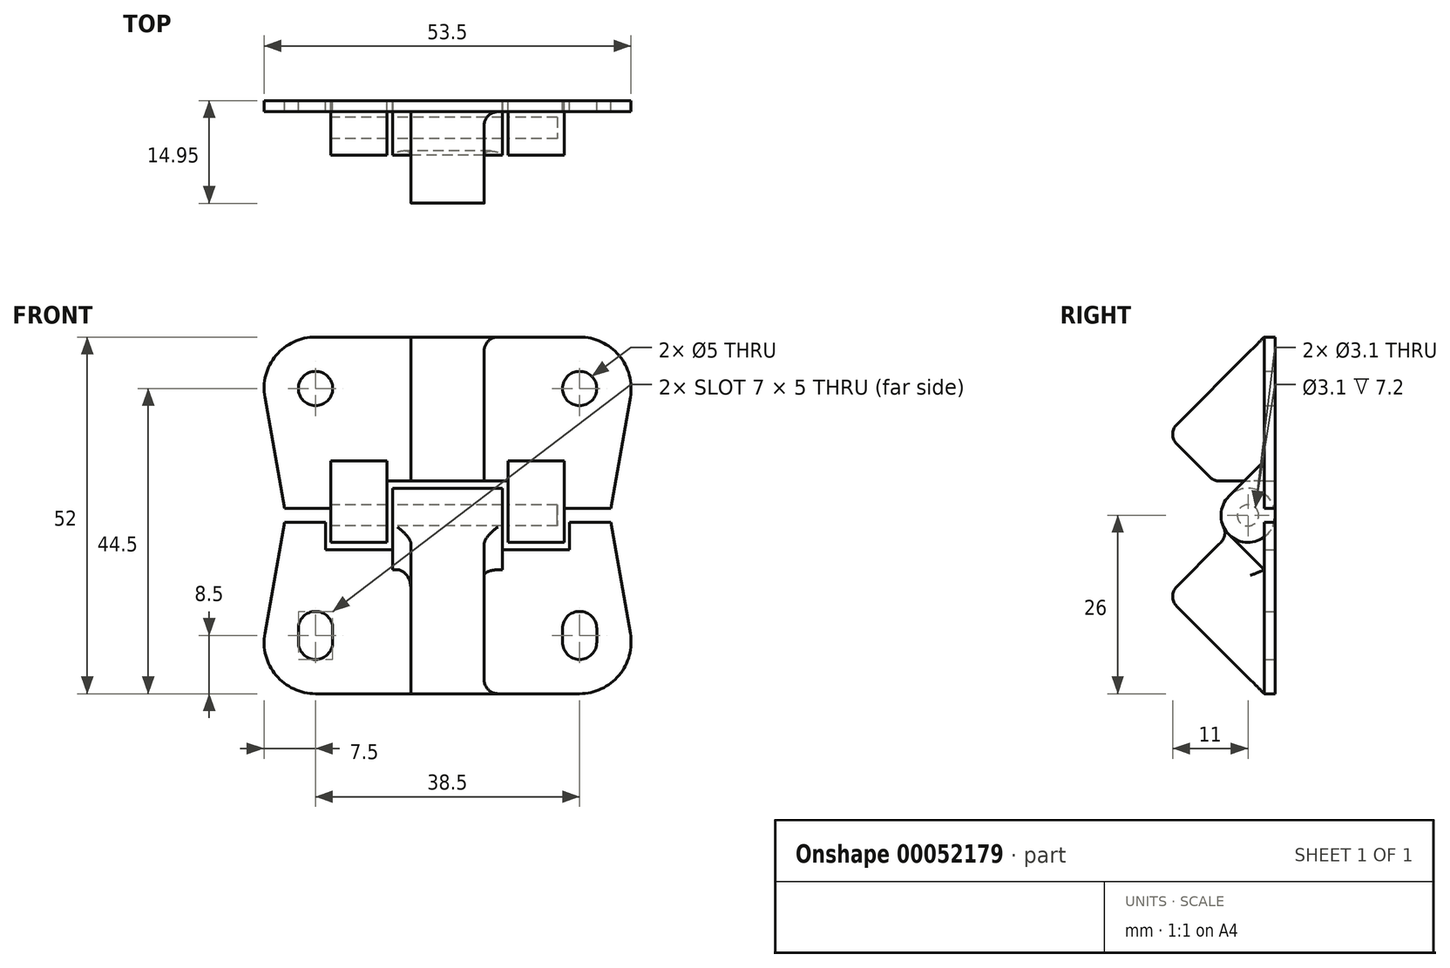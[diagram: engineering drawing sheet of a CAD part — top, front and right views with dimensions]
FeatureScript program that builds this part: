
annotation { "Feature Type Name" : "Feature", "Feature Type Description" : "" }
export const myFeature = defineFeature(function(context is Context, id is Id, definition is map)
    precondition{}
    {
        {
            assignVariable(context, id + "F0", {"name" : "pin_length", "anyValue" : 32});
        }
        {
            var Q0;
            Q0=qCreatedBy(makeId("Front.planeOp"),FACE);
            var sketch = newSketch(context, id + "F1", { "sketchPlane" : qUnion([Q0])});
            skCircle(sketch, "E0", {"center": v(0, 0) * mm, "radius": 2.5 * mm});
            skCircle(sketch, "E1", {"center": v(-38.5, 0) * mm, "radius": 2.5 * mm});
            skArc(sketch, "E2", {"start": v(2.5, -35) * mm, "mid": v(0, -32.5) * mm, "end": v(-2.5, -35) * mm});
            skArc(sketch, "E3", {"start": v(-36, -35) * mm, "mid": v(-38.5, -32.5) * mm, "end": v(-41, -35) * mm});
            skArc(sketch, "E4", {"start": v(-41, -37) * mm, "mid": v(-38.5, -39.5) * mm, "end": v(-36, -37) * mm});
            skArc(sketch, "E5", {"start": v(-2.5, -37) * mm, "mid": v(0, -39.5) * mm, "end": v(2.5, -37) * mm});
            skLineSegment(sketch, "E6", {"start": v(-41, -35) * mm, "end": v(-41, -37) * mm});
            skLineSegment(sketch, "E7", {"start": v(-36, -35) * mm, "end": v(-36, -37) * mm});
            skLineSegment(sketch, "E8", {"start": v(-2.5, -35) * mm, "end": v(-2.5, -37) * mm});
            skLineSegment(sketch, "E9", {"start": v(2.5, -35) * mm, "end": v(2.5, -37) * mm});
            skLineSegment(sketch, "E10", {"start": v(-38.5, 7.5) * mm, "end": v(0, 7.5) * mm});
            skLineSegment(sketch, "E11", {"start": v(0, -44.5) * mm, "end": v(-38.5, -44.5) * mm});
            skLineSegment(sketch, "E12", {"start": v(-45.89, -1.3) * mm, "end": v(-43.03, -17.5) * mm});
            skLineSegment(sketch, "E13", {"start": v(-42.85, -18.5) * mm, "end": v(-43.03, -19.5) * mm});
            skLineSegment(sketch, "E14", {"start": v(7.39, -1.3) * mm, "end": v(4.35, -18.5) * mm});
            skLineSegment(sketch, "E15", {"start": v(4.35, -18.5) * mm, "end": v(7.39, -35.7) * mm});
            skPoint(sketch, "E16.visualSharp", {"position": v(-47.44, 7.5) * mm});
            skArc(sketch, "E16.filletArc", {"start": v(-38.5, 7.5) * mm, "mid": v(-44.25, 4.82) * mm, "end": v(-45.89, -1.3) * mm});
            skPoint(sketch, "E17.visualSharp", {"position": v(-47.44, -44.5) * mm});
            skArc(sketch, "E17.filletArc", {"start": v(-45.89, -35.7) * mm, "mid": v(-44.25, -41.82) * mm, "end": v(-38.5, -44.5) * mm});
            skPoint(sketch, "E18.visualSharp", {"position": v(8.94, -44.5) * mm});
            skArc(sketch, "E18.filletArc", {"start": v(0, -44.5) * mm, "mid": v(5.75, -41.82) * mm, "end": v(7.39, -35.7) * mm});
            skPoint(sketch, "E19.visualSharp", {"position": v(8.94, 7.5) * mm});
            skArc(sketch, "E19.filletArc", {"start": v(7.39, -1.3) * mm, "mid": v(5.75, 4.82) * mm, "end": v(0, 7.5) * mm});
            skLineSegment(sketch, "E20", {"start": v(-42.85, -18.5) * mm, "end": v(4.35, -18.5) * mm, "construction": true});
            skLineSegment(sketch, "E21", {"start": v(-43.03, -17.5) * mm, "end": v(4.53, -17.5) * mm});
            skLineSegment(sketch, "E22", {"start": v(4.53, -19.5) * mm, "end": v(-43.03, -19.5) * mm});
            skLineSegment(sketch, "E23", {"start": v(-43.03, -17.5) * mm, "end": v(-42.85, -18.5) * mm});
            skLineSegment(sketch, "E24", {"start": v(-43.03, -19.5) * mm, "end": v(-45.89, -35.7) * mm});
            skLineSegment(sketch, "E25", {"start": v(-19.25, 7.5) * mm, "end": v(-19.25, -44.5) * mm, "construction": true});
            skLineSegment(sketch, "E26.bottom", {"start": v(-28.05, -17.5) * mm, "end": v(-10.45, -17.5) * mm});
            skLineSegment(sketch, "E26.top", {"start": v(-28.05, -13.5) * mm, "end": v(-19.25, -13.5) * mm});
            skLineSegment(sketch, "E26.left", {"start": v(-28.05, -17.5) * mm, "end": v(-28.05, -13.5) * mm});
            skLineSegment(sketch, "E26.right", {"start": v(-10.45, -17.5) * mm, "end": v(-10.45, -13.5) * mm});
            skLineSegment(sketch, "E27", {"start": v(-19.25, -13.5) * mm, "end": v(-10.45, -13.5) * mm});
            skLineSegment(sketch, "E28.bottom", {"start": v(-37.05, -19.5) * mm, "end": v(-1.45, -19.5) * mm});
            skLineSegment(sketch, "E28.top", {"start": v(-37.05, -23.5) * mm, "end": v(-19.25, -23.5) * mm});
            skLineSegment(sketch, "E28.left", {"start": v(-37.05, -19.5) * mm, "end": v(-37.05, -23.5) * mm});
            skLineSegment(sketch, "E28.right", {"start": v(-1.45, -19.5) * mm, "end": v(-1.45, -23.5) * mm});
            skLineSegment(sketch, "E29", {"start": v(-19.25, -23.5) * mm, "end": v(-1.45, -23.5) * mm});
            skSolve(sketch);
        }
        {
            var Q0;
            Q0=makeQuery(id+"F1.imprint","IMPRINT",FACE,{"disambiguationData":[TD([[makeQuery(id+"F1.imprint","IMPRINT",EDGE,{"derivedFrom":sQuery(id+"F1.wireOp",EDGE,"E0")}),-1.0]])]});
            var Q1;
            Q1=makeQuery(id+"F1.imprint","IMPRINT",FACE,{"disambiguationData":[TD([[makeQuery(id+"F1.imprint","IMPRINT",EDGE,{"derivedFrom":sQuery(id+"F1.wireOp",EDGE,"E2")}),-1.0]])]});
            extrude(context, id + "F2", {"entities" : qUnion([Q0, Q1]), "depth" : (0.4 * 4) * mm});
        }
        {
            var Q0;
            Q0=sQuery(id+"F1.wireOp",EDGE,"E25");
            var Q1;
            Q1=qCreatedBy(makeId("Right.planeOp"),FACE);
            cPlane(context, id + "F3", {"entities" : qUnion([Q0, Q1]), "cplaneType" : CPlaneType.LINE_ANGLE, "offset" : 150 * mm, "angle" : 180 * degree, "width" : 150 * mm, "height" : 150 * mm});
        }
        {
            var Q0;
            Q0=qCreatedBy(id+"F3.planeOp",FACE);
            var sketch = newSketch(context, id + "F4", { "sketchPlane" : qUnion([Q0])});
            skCircle(sketch, "E30", {"center": v(-3.95, -18.5) * mm, "radius": 3.95 * mm});
            skCircle(sketch, "E31", {"center": v(-3.95, -18.5) * mm, "radius": 1.55 * mm});
            skSolve(sketch);
        }
        {
            var Q0;
            Q0=makeQuery(id+"F4.imprint","IMPRINT",FACE,{"disambiguationData":[TD([[makeQuery(id+"F4.imprint","IMPRINT",EDGE,{"derivedFrom":sQuery(id+"F4.wireOp",EDGE,"E30")}),1.0]])]});
            extrude(context, id + "F5", {"entities" : qUnion([Q0]), "endBound" : BoundingType.SYMMETRIC, "depth" : (getVariable(context, 'pin_length') + 2) * mm});
        }
        {
            var Q0;
            Q0=makeQuery(id+"F4.imprint","IMPRINT",FACE,{"disambiguationData":[TD([[makeQuery(id+"F4.imprint","IMPRINT",EDGE,{"derivedFrom":sQuery(id+"F4.wireOp",EDGE,"E30")}),1.0]])]});
            extrude(context, id + "F6", {"entities" : qUnion([Q0]), "endBound" : BoundingType.SYMMETRIC, "depth" : (getVariable(context, 'pin_length') / 2) * mm});
        }
        {
            var Q0;
            Q0=makeQuery(id+"F6.opExtrude","SWEPT_BODY",BODY,{"disambiguationData":[OSD([sQuery(id+"F4.wireOp",EDGE,"E30"),sQuery(id+"F4.wireOp",EDGE,"E31")])]});
            var Q1;
            Q1=makeQuery(id+"F5.opExtrude","SWEPT_BODY",BODY,{"disambiguationData":[OSD([sQuery(id+"F4.wireOp",EDGE,"E30"),sQuery(id+"F4.wireOp",EDGE,"E31")])]});
            booleanBodies(context, id + "F7", {"operationType" : BooleanOperationType.SUBTRACTION, "tools" : qUnion([Q0]), "targets" : qUnion([Q1]), "offset" : true, "offsetAll" : true, "offsetDistance" : .8 * mm, "keepTools" : true});
        }
        {
            var Q0;
            Q0=makeQuery(id+"F5.opExtrude","CAP_FACE",FACE,{"disambiguationData":[OSD([sQuery(id+"F4.wireOp",EDGE,"E30"),sQuery(id+"F4.wireOp",EDGE,"E31")])],"isStart":false});
            var sketch = newSketch(context, id + "F8", { "sketchPlane" : qUnion([Q0])});
            skLineSegment(sketch, "E32", {"start": v(0, -18.5) * mm, "end": v(0, -8.96) * mm});
            skLineSegment(sketch, "E33", {"start": v(0, -8.96) * mm, "end": v(-6.74, -15.7) * mm});
            skLineSegment(sketch, "E34", {"start": v(-3.95, -18.5) * mm, "end": v(4.49, -18.5) * mm, "construction": true});
            skLineSegment(sketch, "E35", {"start": v(-6.74, -21.3) * mm, "end": v(0, -28.04) * mm});
            skLineSegment(sketch, "E36", {"start": v(0, -28.04) * mm, "end": v(0, -18.5) * mm});
            skCircle(sketch, "E37", {"center": v(-3.95, -18.5) * mm, "radius": 1.55 * mm});
            skSolve(sketch);
        }
        {
            var Q0;
            {var subQ6=sQuery(id+"F8.wireOp",EDGE,"E32");Q0=makeQuery(id+"F8.imprint","IMPRINT",FACE,{"disambiguationData":[TD([[makeQuery(id+"F8.imprint","IMPRINT",EDGE,{"derivedFrom":subQ6}),1.0]])]});}
            var Q1;
            Q1=makeQuery(id+"F7.tempBoolean.opBoolean","COPY",FACE,{"derivedFrom":makeQuery(id+"F7.offsetTempBody.opPattern","COPY",FACE,{"derivedFrom":makeQuery(id+"F6.opExtrude","CAP_FACE",FACE,{"disambiguationData":[OSD([sQuery(id+"F4.wireOp",EDGE,"E30"),sQuery(id+"F4.wireOp",EDGE,"E31")])],"isStart":false}),"instanceName":"1"})});
            var Q2;
            Q2=makeQuery(id+"F2.opExtrude","SWEPT_BODY",BODY,{"disambiguationData":[OSD([sQuery(id+"F1.wireOp",EDGE,"E0"),sQuery(id+"F1.wireOp",EDGE,"E1"),sQuery(id+"F1.wireOp",EDGE,"E10"),sQuery(id+"F1.wireOp",EDGE,"E12"),sQuery(id+"F1.wireOp",EDGE,"E14"),sQuery(id+"F1.wireOp",EDGE,"E16.filletArc"),sQuery(id+"F1.wireOp",EDGE,"E19.filletArc"),sQuery(id+"F1.wireOp",EDGE,"E21")])]});
            var Q3;
            Q3=makeQuery(id+"F5.opExtrude","CAP_FACE",FACE,{"disambiguationData":[OSD([sQuery(id+"F4.wireOp",EDGE,"E30"),sQuery(id+"F4.wireOp",EDGE,"E31")])],"isStart":true});
            extrude(context, id + "F9", {"entities" : qUnion([Q0]), "operationType" : NewBodyOperationType.ADD, "endBound" : BoundingType.UP_TO_SURFACE, "oppositeDirection" : true, "endBoundEntityFace" : qUnion([Q1]), "endBoundEntityBody" : qUnion([Q2]), "depth" : 25 * mm});
        }
        {
            var Q0;
            {var subQ6=sQuery(id+"F8.wireOp",EDGE,"E32");Q0=makeQuery(id+"F8.imprint","IMPRINT",FACE,{"disambiguationData":[TD([[makeQuery(id+"F8.imprint","IMPRINT",EDGE,{"derivedFrom":subQ6}),1.0]])]});}
            var Q1;
            Q1=makeQuery(id+"F5.opExtrude","CAP_FACE",FACE,{"disambiguationData":[OSD([sQuery(id+"F4.wireOp",EDGE,"E30"),sQuery(id+"F4.wireOp",EDGE,"E31")])],"isStart":true});
            var Q2;
            Q2=makeQuery(id+"F7.tempBoolean.opBoolean","COPY",FACE,{"derivedFrom":makeQuery(id+"F7.offsetTempBody.opPattern","COPY",FACE,{"derivedFrom":makeQuery(id+"F6.opExtrude","CAP_FACE",FACE,{"disambiguationData":[OSD([sQuery(id+"F4.wireOp",EDGE,"E30"),sQuery(id+"F4.wireOp",EDGE,"E31")])],"isStart":true}),"instanceName":"1"})});
            extrude(context, id + "F10", {"entities" : qUnion([Q0]), "operationType" : NewBodyOperationType.ADD, "endBound" : BoundingType.UP_TO_SURFACE, "oppositeDirection" : true, "endBoundEntityFace" : qUnion([Q1]), "depth" : 25 * mm, "hasSecondDirection" : true, "secondDirectionBound" : SecondDirectionBoundingType.UP_TO_SURFACE, "secondDirectionOppositeDirection" : true, "secondDirectionBoundEntityFace" : qUnion([Q2]), "secondDirectionDepth" : 45.6 * mm});
        }
        {
            var Q0;
            {var subQ0=sQuery(id+"F8.wireOp",EDGE,"E35");Q0=makeQuery(id+"F8.imprint","IMPRINT",FACE,{"disambiguationData":[TD([[makeQuery(id+"F8.imprint","IMPRINT",EDGE,{"derivedFrom":subQ0}),1.0]])]});}
            var Q1;
            Q1=makeQuery(id+"F6.opExtrude","CAP_FACE",FACE,{"disambiguationData":[OSD([sQuery(id+"F4.wireOp",EDGE,"E30"),sQuery(id+"F4.wireOp",EDGE,"E31")])],"isStart":true});
            var Q2;
            Q2=makeQuery(id+"F6.opExtrude","CAP_FACE",FACE,{"disambiguationData":[OSD([sQuery(id+"F4.wireOp",EDGE,"E30"),sQuery(id+"F4.wireOp",EDGE,"E31")])],"isStart":false});
            extrude(context, id + "F11", {"entities" : qUnion([Q0]), "operationType" : NewBodyOperationType.ADD, "endBound" : BoundingType.UP_TO_SURFACE, "oppositeDirection" : true, "endBoundEntityFace" : qUnion([Q1]), "depth" : 25 * mm, "hasSecondDirection" : true, "secondDirectionBound" : SecondDirectionBoundingType.UP_TO_SURFACE, "secondDirectionOppositeDirection" : true, "secondDirectionBoundEntityFace" : qUnion([Q2]), "secondDirectionDepth" : 25 * mm});
        }
        {
            var Q0;
            Q0=makeQuery(id+"F8.imprint","IMPRINT",FACE,{"disambiguationData":[TD([[makeQuery(id+"F8.imprint","IMPRINT",EDGE,{"derivedFrom":sQuery(id+"F8.wireOp",EDGE,"E37")}),1.0]])]});
            extrude(context, id + "F12", {"entities" : qUnion([Q0]), "operationType" : NewBodyOperationType.ADD, "oppositeDirection" : true, "depth" : 1 * mm});
        }
        {
            var Q0;
            Q0=qCreatedBy(id+"F3.planeOp",FACE);
            var sketch = newSketch(context, id + "F13", { "sketchPlane" : qUnion([Q0])});
            skLineSegment(sketch, "E38", {"start": v(-3.95, -18.5) * mm, "end": v(-15.78, -6.68) * mm});
            skLineSegment(sketch, "E39", {"start": v(-15.77, -30.33) * mm, "end": v(-3.95, -18.5) * mm});
            skLineSegment(sketch, "E40", {"start": v(-1.6, 7.5) * mm, "end": v(-15.78, -6.68) * mm});
            skLineSegment(sketch, "E41", {"start": v(-1.6, -44.5) * mm, "end": v(-15.77, -30.33) * mm});
            skLineSegment(sketch, "E42", {"start": v(-8.95, -13.5) * mm, "end": v(-1.6, -13.5) * mm});
            skLineSegment(sketch, "E43", {"start": v(-1.6, 7.5) * mm, "end": v(-1.6, -13.5) * mm});
            skLineSegment(sketch, "E44", {"start": v(-6.74, -21.3) * mm, "end": v(-1.6, -21.3) * mm});
            skLineSegment(sketch, "E45", {"start": v(-1.6, -21.3) * mm, "end": v(-1.6, -44.5) * mm});
            skSolve(sketch);
        }
        {
            var Q0;
            {var subQ0=sQuery(id+"F13.wireOp",EDGE,"E40");Q0=makeQuery(id+"F13.imprint","IMPRINT",FACE,{"disambiguationData":[TD([[makeQuery(id+"F13.imprint","IMPRINT",EDGE,{"derivedFrom":subQ0}),1.0]])]});}
            var Q1;
            {var subQ0=sQuery(id+"F13.wireOp",EDGE,"E41");Q1=makeQuery(id+"F13.imprint","IMPRINT",FACE,{"disambiguationData":[TD([[makeQuery(id+"F13.imprint","IMPRINT",EDGE,{"derivedFrom":subQ0}),-1.0]])]});}
            extrude(context, id + "F14", {"entities" : qUnion([Q0, Q1]), "operationType" : NewBodyOperationType.ADD, "endBound" : BoundingType.SYMMETRIC, "depth" : (getVariable(context, 'pin_length') / 3) * mm});
        }
        {
            var Q0;
            Q0=makeQuery(id+"F14.opExtrude","SWEPT_EDGE",EDGE,{"disambiguationData":[OSD([sQuery(id+"F13.wireOp",EDGE,"E39"),sQuery(id+"F13.wireOp",EDGE,"E41")])]});
            var Q1;
            Q1=makeQuery(id+"F14.opExtrude","SWEPT_EDGE",EDGE,{"disambiguationData":[OSD([sQuery(id+"F13.wireOp",EDGE,"E38"),sQuery(id+"F13.wireOp",EDGE,"E42")])]});
            var Q2;
            Q2=makeQuery(id+"F14.opExtrude","SWEPT_EDGE",EDGE,{"disambiguationData":[OSD([sQuery(id+"F13.wireOp",EDGE,"E38"),sQuery(id+"F13.wireOp",EDGE,"E40")])]});
            var Q3;
            Q3=makeQuery(id+"F14.opExtrude","CAP_EDGE",EDGE,{"disambiguationData":[OSD([sQuery(id+"F13.wireOp",EDGE,"E43")])],"isStart":false});
            var Q4;
            Q4=makeQuery(id+"F14.opExtrude","CAP_EDGE",EDGE,{"disambiguationData":[OSD([sQuery(id+"F13.wireOp",EDGE,"E43")])],"isStart":true});
            var Q5;
            Q5=makeQuery(id+"F14.opExtrude","CAP_EDGE",EDGE,{"disambiguationData":[OSD([sQuery(id+"F13.wireOp",EDGE,"E45")])],"isStart":true});
            var Q6;
            Q6=makeQuery(id+"F14.boolean.opBoolean","INTERSECT",EDGE,{"derivedFrom":[makeQuery(id+"F11.opExtrude","SWEPT_FACE",FACE,{"disambiguationData":[OSD([sQuery(id+"F8.wireOp",EDGE,"E35")])]}),makeQuery(id+"F14.opExtrude","CAP_FACE",FACE,{"disambiguationData":[OSD([sQuery(id+"F13.wireOp",EDGE,"E39"),sQuery(id+"F13.wireOp",EDGE,"E41"),sQuery(id+"F13.wireOp",EDGE,"E44"),sQuery(id+"F13.wireOp",EDGE,"E45")])],"isStart":true})]});
            var Q7;
            Q7=makeQuery(id+"F14.boolean.opBoolean","INTERSECT",EDGE,{"derivedFrom":[makeQuery(id+"F11.opExtrude","SWEPT_FACE",FACE,{"disambiguationData":[OSD([sQuery(id+"F8.wireOp",EDGE,"E35")])]}),makeQuery(id+"F14.opExtrude","CAP_FACE",FACE,{"disambiguationData":[OSD([sQuery(id+"F13.wireOp",EDGE,"E39"),sQuery(id+"F13.wireOp",EDGE,"E41"),sQuery(id+"F13.wireOp",EDGE,"E44"),sQuery(id+"F13.wireOp",EDGE,"E45")])],"isStart":false})]});
            var Q8;
            Q8=makeQuery(id+"F14.opExtrude","CAP_EDGE",EDGE,{"disambiguationData":[OSD([sQuery(id+"F13.wireOp",EDGE,"E45")])],"isStart":false});
            var Q9;
            Q9=makeQuery(id+"F14.opExtrude","SWEPT_EDGE",EDGE,{"disambiguationData":[OSD([sQuery(id+"F13.wireOp",EDGE,"E39"),sQuery(id+"F13.wireOp",EDGE,"E44")])]});
            fillet(context, id + "F15", {"entities" : qUnion([Q0, Q1, Q2, Q3, Q4, Q5, Q6, Q7, Q8, Q9]), "radius" : 2 * mm, "tangentPropagation" : true, "allowEdgeOverflow" : false});
        }
    });
